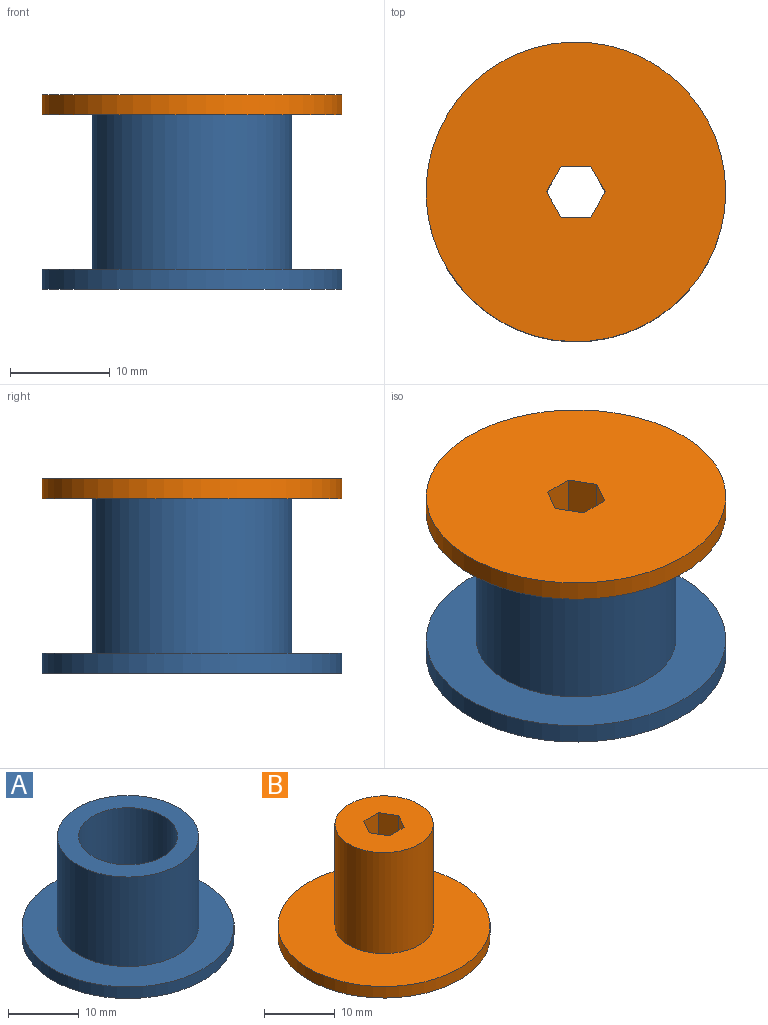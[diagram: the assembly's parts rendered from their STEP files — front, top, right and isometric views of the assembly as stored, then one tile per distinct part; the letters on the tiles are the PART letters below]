
ASSEMBLY  parts=2 mates=1
PART A: 6 faces, bbox 30x30x17.5 mm
  f0: cylinder r=15mm len=30mm, axis (0,0,1), area 188.5mm2, adj f1,f2
  f1: plane 30x30mm, normal (0,0,-1), area 552.9mm2, adj f0,f5
  f2: plane 30x30mm, normal (0,0,1), area 392.7mm2, adj f0,f3
  f3: cylinder r=10mm len=20mm, axis (0,0,-1), area 973.9mm2, adj f2,f4
  f4: plane 20x20mm, normal (0,0,1), area 160.2mm2, adj f3,f5
  f5: cylinder r=7mm len=17.5mm, axis (0,0,1), area 769.7mm2, adj f1,f4
PART B: 11 faces, bbox 30x30x19.5 mm
  f0: cylinder r=15mm len=30mm, axis (0,0,1), area 188.5mm2, adj f1,f2
  f1: plane 30x30mm, normal (0,0,-1), area 684.3mm2, adj f0,f3,f4,f5,f6,f7,f8
  f2: plane 30x30mm, normal (0,0,1), area 555.1mm2, adj f0,f9
  f3: plane 19.5x2.55mm, normal (0.87,-0.5,0), area 57.4mm2, adj f1,f4,f8,f10
  f4: plane 19.5x2.94mm, normal (0,-1,0), area 57.4mm2, adj f1,f3,f5,f10
  f5: plane 19.5x2.55mm, normal (-0.87,-0.5,0), area 57.4mm2, adj f1,f4,f6,f10
  f6: plane 19.5x2.55mm, normal (-0.87,0.5,0), area 57.4mm2, adj f1,f5,f7,f10
  f7: plane 19.5x2.94mm, normal (0,1,0), area 57.4mm2, adj f1,f6,f8,f10
  f8: plane 19.5x2.55mm, normal (0.87,0.5,0), area 57.4mm2, adj f1,f3,f7,f10
  f9: cylinder r=6.95mm len=17.5mm, axis (0,0,-1), area 764.2mm2, adj f2,f10
  f10: plane 13.9x13.9mm, normal (0,0,1), area 129.2mm2, adj f3,f4,f5,f6,f7,f8,f9
PLACE A t=(-15.37,-0.36,6.02)mm
PLACE B rot(axis=(1,0,0),180deg) t=(-15.37,-0.36,21.52)mm
MATE fastened B.f9 <-> A.f5  axis (0,0,-1) through (-15.37,-0.36,21.52)mm
